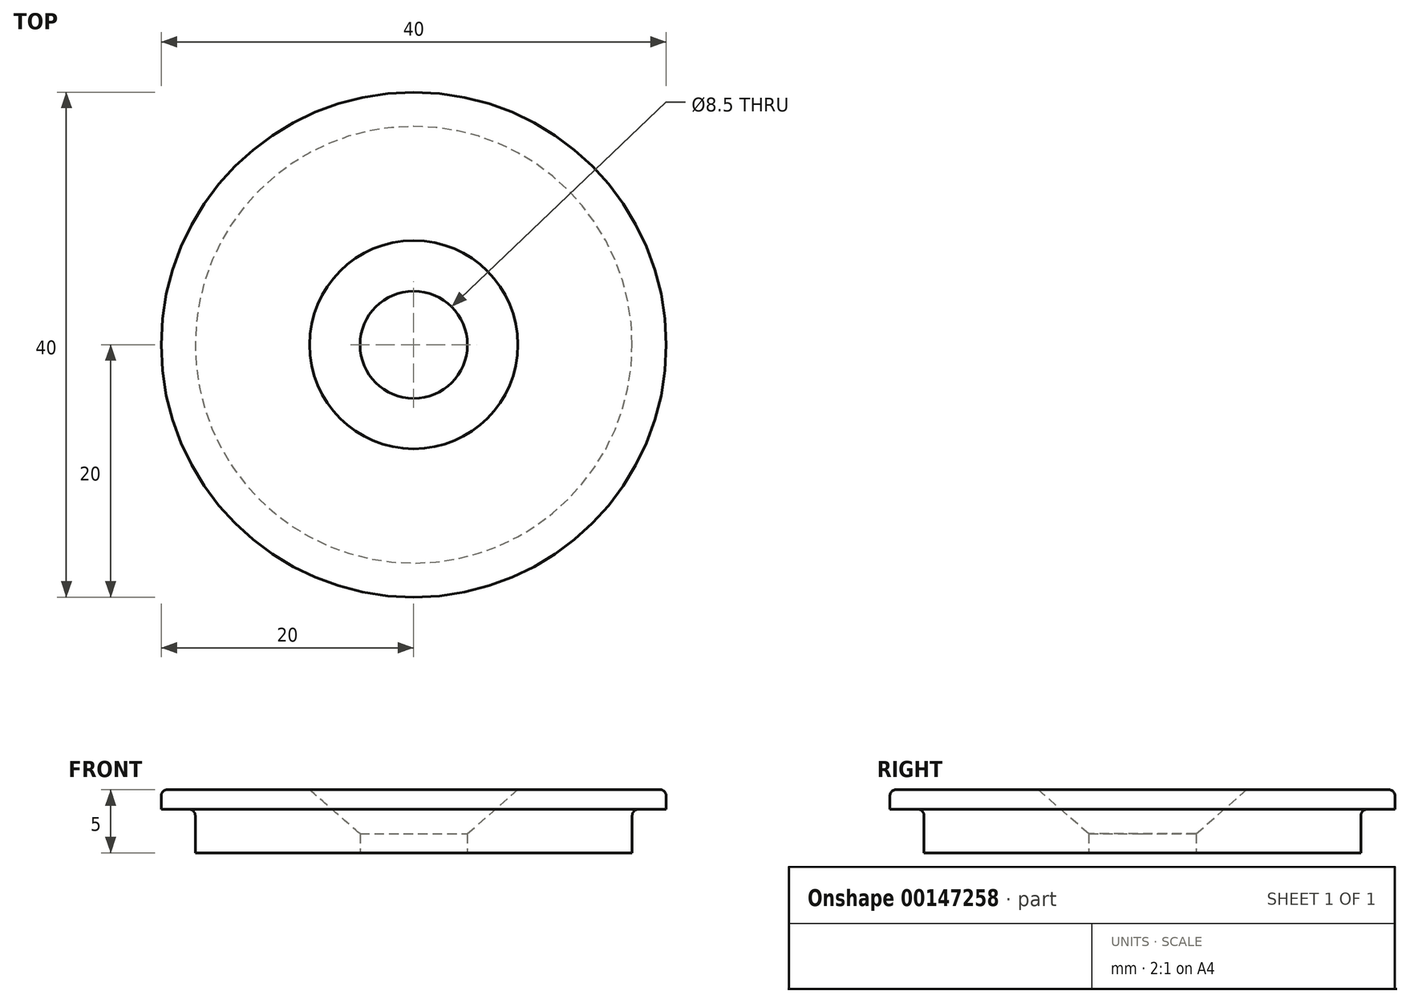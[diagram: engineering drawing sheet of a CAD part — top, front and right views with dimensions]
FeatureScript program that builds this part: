
annotation { "Feature Type Name" : "Feature", "Feature Type Description" : "" }
export const myFeature = defineFeature(function(context is Context, id is Id, definition is map)
    precondition{}
    {
        {
            var Q0;
            Q0=qCreatedBy(makeId("Right.planeOp"),FACE);
            var sketch = newSketch(context, id + "F0", { "sketchPlane" : qUnion([Q0])});
            skLineSegment(sketch, "E0", {"start": v(0, 0) * mm, "end": v(0, 5) * mm, "construction": true});
            skLineSegment(sketch, "E1", {"start": v(-20, 0) * mm, "end": v(-20, 5) * mm, "construction": true});
            skLineSegment(sketch, "E2", {"start": v(-17.3, 0) * mm, "end": v(-17.3, 5) * mm, "construction": true});
            skLineSegment(sketch, "E3", {"start": v(-4.25, 0) * mm, "end": v(-17.3, 0) * mm});
            skPoint(sketch, "E4", {"position": v(-4.25, 0) * mm});
            skPoint(sketch, "E5", {"position": v(-8.25, 5) * mm});
            skLineSegment(sketch, "E6", {"start": v(-4.25, 0) * mm, "end": v(-4.25, 1.5) * mm});
            skLineSegment(sketch, "E7", {"start": v(-4.25, 1.5) * mm, "end": v(-8.25, 5) * mm});
            skLineSegment(sketch, "E8", {"start": v(-8.25, 5) * mm, "end": v(-19.5, 5) * mm});
            skLineSegment(sketch, "E9", {"start": v(-17.3, 0) * mm, "end": v(-17.3, 2.95) * mm});
            skLineSegment(sketch, "E10", {"start": v(-17.8, 3.45) * mm, "end": v(-20, 3.45) * mm});
            skLineSegment(sketch, "E11", {"start": v(-20, 3.45) * mm, "end": v(-20, 4.5) * mm});
            skPoint(sketch, "E12.visualSharp", {"position": v(-20, 5) * mm});
            skArc(sketch, "E12.filletArc", {"start": v(-19.5, 5) * mm, "mid": v(-19.85, 4.85) * mm, "end": v(-20, 4.5) * mm});
            skPoint(sketch, "E13.visualSharp", {"position": v(-17.3, 3.45) * mm});
            skArc(sketch, "E13.filletArc", {"start": v(-17.3, 2.95) * mm, "mid": v(-17.45, 3.3) * mm, "end": v(-17.8, 3.45) * mm});
            skSolve(sketch);
        }
        {
            var Q0;
            Q0=makeQuery(id+"F0.imprint","IMPRINT",FACE,{"disambiguationData":[TD([[makeQuery(id+"F0.imprint","IMPRINT",EDGE,{"derivedFrom":sQuery(id+"F0.wireOp",EDGE,"E3")}),-1.0]])]});
            var Q1;
            Q1=sQuery(id+"F0.wireOp",EDGE,"E0");
            revolve(context, id + "F1", {"entities" : qUnion([Q0]), "axis" : qUnion([Q1]), "revolveType" : RevolveType.FULL});
        }
    });
